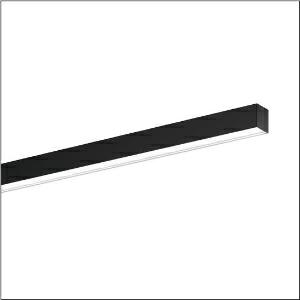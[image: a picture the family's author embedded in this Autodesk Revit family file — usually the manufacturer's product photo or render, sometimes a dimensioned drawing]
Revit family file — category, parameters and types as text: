
# Revit family: silica_r__21_51mx20da42bb_071f
name_source: partatom
category: Lighting Fixtures
units: mm (PartAtom-declared; Revit-internal decimal feet)

## family parameters
Cut with Voids When Loaded = No
Host = Face
Light Source = No
Part Type = Normal
Room Calculation Point = No
Round Connector Dimension = Use Diameter
Shared = No

## types (1)
- --- (1 x LED, 2400 lm, 15.2 W, 4000K)
    Apparent Load = 15 VA
    CIE Flux Codes = 48 79 96 100 100
    Color Rendering = 80
    Color Temperature = 4000K
    Default Elevation = 1800 mm
    Description = Silica® 21, office luminaire, primary optical cover: cover, of PMMA, opal, light emission: direct distribution, primary light characteristic: symmetric, installation type: surface-mounted, LED, rated luminous flux: 2.400lm, luminous efficacy: 158lm/W, light colour: 840, colour temperature: 4000K, with terminal, 3+2-pole, max. 2.5mm², mains connection: 220..240V, AC, 50/60Hz, rated input power: 15.2W, luminaire housing, of aluminium, jet black (RAL 9005), length: 1.204mm, width: 53mm, height: 53mm, protection rating (complete): IP20, insulation class (complete): insulation class I (protective earthing), certification: CE, permissible operating ambient temperature: 0..+35°C, standard: EN 50419, packaging unit: 1 piece
    Height = 0 mm  [stored 0 ft]
    Lamp = 1 x LED
    Lamp Light Flux = 2400 lm
    Lamp Power = 15.2 W
    Lamp count = 1
    Length = 1204 mm
    Luminous efficacy = 158 lm/W
    Manufacturer = Siteco
    ModVariant = No
    Model = 51MX20DA42BB
    Mounting Place = Ceiling
    Mounting Type = Recessed
    Number of Poles = 1
    OnlyDefault = Yes
    Power Factor = 1
    Product Name = Silica® 21
    Product group = office luminaire | ceiling recessed
    ProductGroupID = 401
    Protection Class = Protection class I
    Protection Degree = IP 20
    RLX_Detail_Level = 1
    RLX_Emergency_Light_Flux = 0 lm
    RLX_Emergency_Type = 0
    RLX_Emergency_Type_DB = No
    RlxData = <blob elided: 28757 chars, md5=87aa1fe9>
    Socket = socket
    Standby Power = 0 W
    System Light Flux = 2400 lm
    System Power = 15 W
    Type Comments = factory setting: luminous flux: 100 % | dim-lin: 254 | 218 mA
    Type Image = l_1313584.jpg
    URL = http://relux.com
    VarID = @adj_066527
    Voltage = 0 V
    Weight = 0.00 kg
    Width = 53 mm

note: [stored X ft] marks values corroborated as IEEE doubles in the binary element streams (Revit-internal decimal feet)

## geometry (parser evidence)
native form markers: Blend x4, Sweep x8
no freeform markers — native parametric forms only
